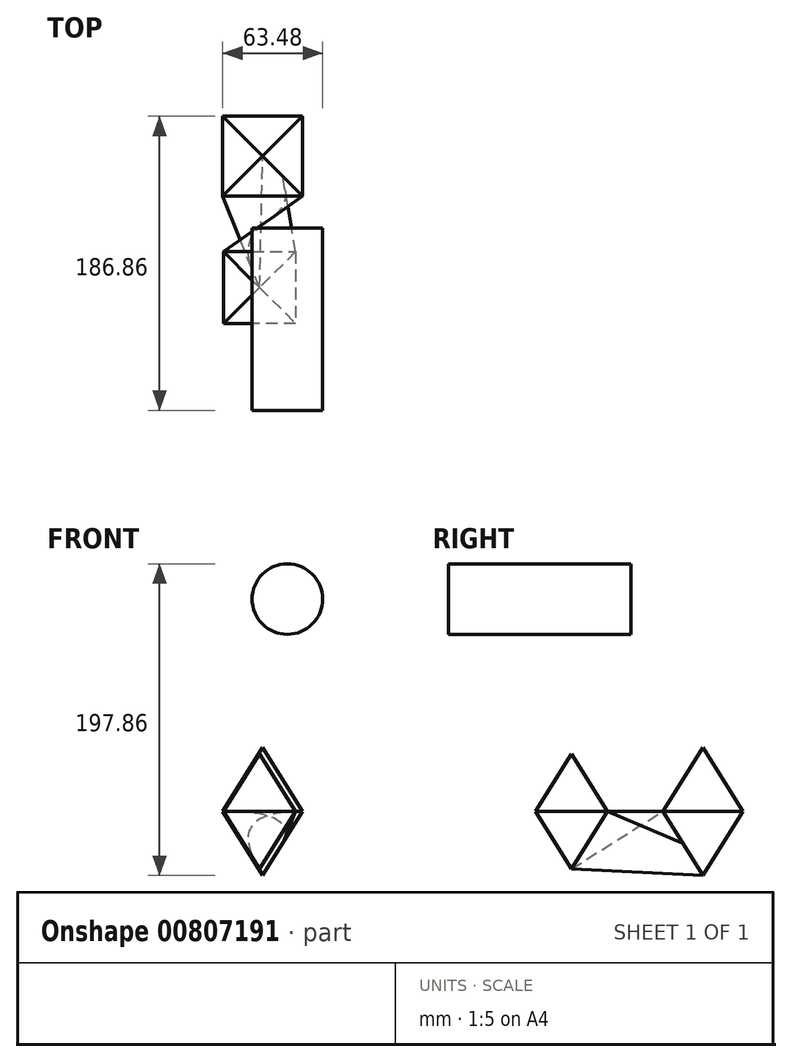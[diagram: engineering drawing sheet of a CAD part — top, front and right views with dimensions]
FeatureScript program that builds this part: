
annotation { "Feature Type Name" : "Feature", "Feature Type Description" : "" }
export const myFeature = defineFeature(function(context is Context, id is Id, definition is map)
    precondition{}
    {
        {
            var Q0;
            Q0=qCreatedBy(makeId("Top.planeOp"),FACE);
            var sketch = newSketch(context, id + "F0", { "sketchPlane" : qUnion([Q0])});
            skLineSegment(sketch, "E0.bottom", {"start": v(26.66, 71.04) * mm, "end": v(-24.14, 71.04) * mm});
            skLineSegment(sketch, "E0.top", {"start": v(26.66, 20.24) * mm, "end": v(-24.14, 20.24) * mm});
            skLineSegment(sketch, "E0.left", {"start": v(26.66, 71.04) * mm, "end": v(26.66, 20.24) * mm});
            skLineSegment(sketch, "E0.right", {"start": v(-24.14, 71.04) * mm, "end": v(-24.14, 20.24) * mm});
            skLineSegment(sketch, "E1.bottom", {"start": v(-23.7, -60.74) * mm, "end": v(22.28, -60.74) * mm});
            skLineSegment(sketch, "E1.top", {"start": v(-23.7, -14.97) * mm, "end": v(22.28, -14.97) * mm});
            skLineSegment(sketch, "E1.left", {"start": v(-23.7, -60.74) * mm, "end": v(-23.7, -14.97) * mm});
            skLineSegment(sketch, "E1.right", {"start": v(22.28, -60.74) * mm, "end": v(22.28, -14.97) * mm});
            skSolve(sketch);
        }
        {
            var Q0;
            Q0=makeQuery(id+"F0.imprint","IMPRINT",FACE,{"disambiguationData":[TD([[makeQuery(id+"F0.imprint","IMPRINT",EDGE,{"derivedFrom":sQuery(id+"F0.wireOp",EDGE,"E0.bottom")}),1.0]])]});
            var Q1;
            Q1=makeQuery(id+"F0.imprint","IMPRINT",FACE,{"disambiguationData":[TD([[makeQuery(id+"F0.imprint","IMPRINT",EDGE,{"derivedFrom":sQuery(id+"F0.wireOp",EDGE,"E1.bottom")}),1.0]])]});
            extrude(context, id + "F1", {"entities" : qUnion([Q0, Q1]), "surfaceOperationType" : NewSurfaceOperationType.ADD, "endBound" : BoundingType.SYMMETRIC, "depth" : 113.8 * mm, "offsetDistance" : 25.4 * mm, "hasDraft" : true, "draftAngle" : 32 * degree, "draftPullDirection" : true, "hasSecondDirection" : true, "secondDirectionOppositeDirection" : true, "secondDirectionDepth" : 25.4 * mm});
        }
        {
            var Q0;
            Q0=qCreatedBy(makeId("Front.planeOp"),FACE);
            var sketch = newSketch(context, id + "F2", { "sketchPlane" : qUnion([Q0])});
            skCircle(sketch, "E2", {"center": v(16.94, 134.82) * mm, "radius": 22.4 * mm});
            skSolve(sketch);
        }
        {
            var Q0;
            Q0=makeQuery(id+"F2.imprint","IMPRINT",FACE,{"disambiguationData":[TD([[makeQuery(id+"F2.imprint","IMPRINT",EDGE,{"derivedFrom":sQuery(id+"F2.wireOp",EDGE,"E2")}),1.0]])]});
            extrude(context, id + "F3", {"entities" : qUnion([Q0]), "depth" : 115.82 * mm, "offsetDistance" : 25.4 * mm});
        }
        {
            var Q0;
            Q0=makeQuery(id+"F1.*.split.splitOp","SPLIT",FACE,{"derivedFrom":makeQuery(id+"F1.opExtrude","SWEPT_FACE",FACE,{"disambiguationData":[OSD([sQuery(id+"F0.wireOp",EDGE,"E1.top")])]}),"isFromBackBody":true});
            var Q1;
            Q1=makeQuery(id+"F1.*.split.splitOp","SPLIT",FACE,{"derivedFrom":makeQuery(id+"F1.opExtrude","SWEPT_FACE",FACE,{"disambiguationData":[OSD([sQuery(id+"F0.wireOp",EDGE,"E0.top")])]}),"isFromBackBody":true});
            loft(context, id + "F4", {"sheetProfilesArray" : [{ "sheetProfileEntities" : qUnion([Q0]) }, { "sheetProfileEntities" : qUnion([Q1]) }]});
        }
    });
